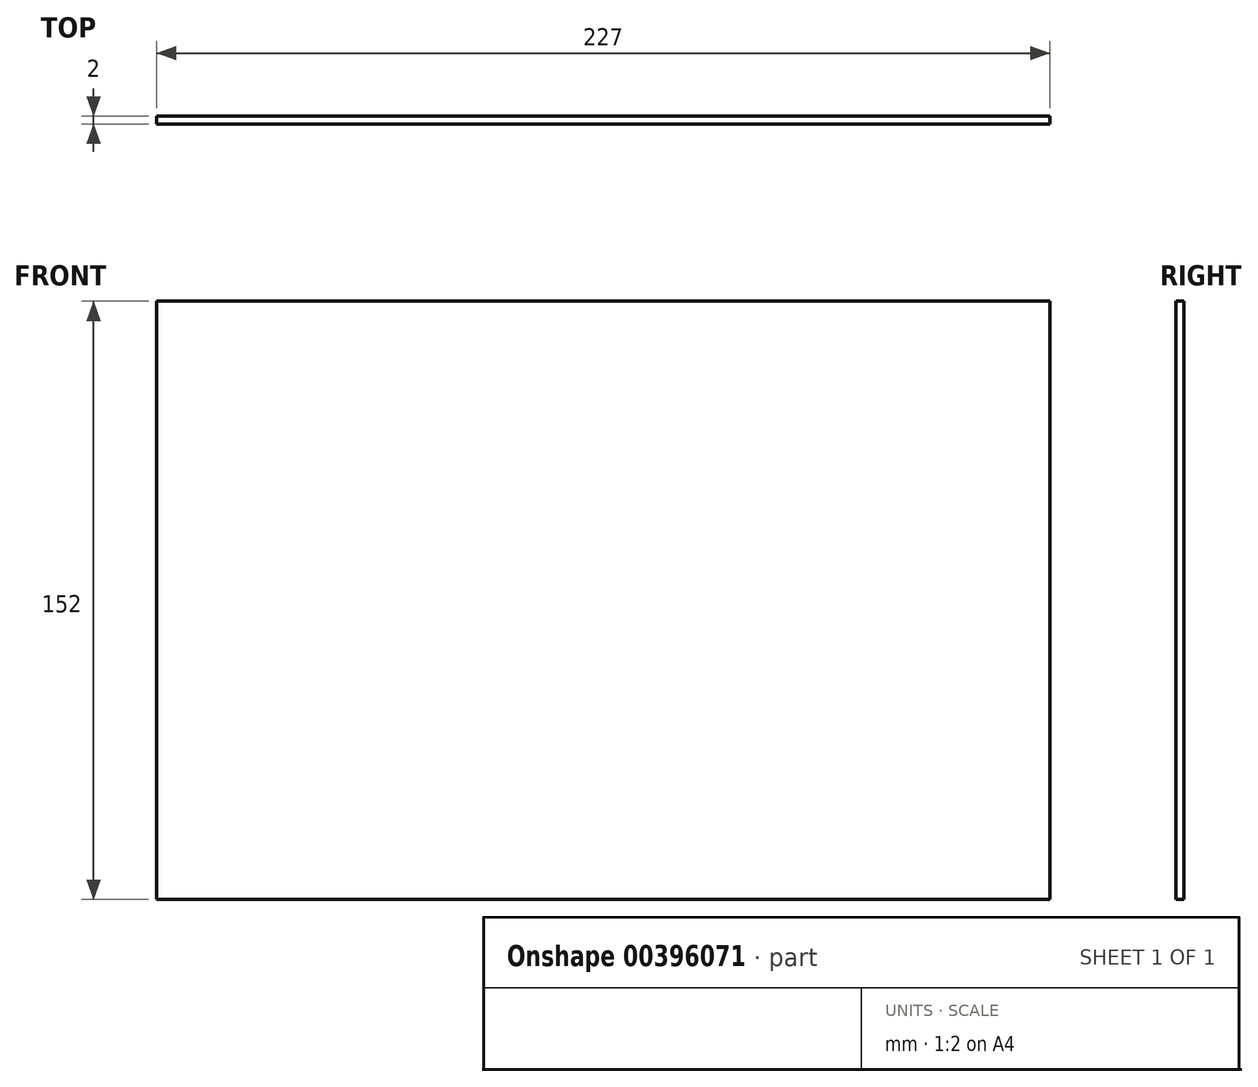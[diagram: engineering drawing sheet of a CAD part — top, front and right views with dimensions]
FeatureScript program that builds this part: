
annotation { "Feature Type Name" : "Feature", "Feature Type Description" : "" }
export const myFeature = defineFeature(function(context is Context, id is Id, definition is map)
    precondition{}
    {
        {
            var Q0;
            Q0=qCreatedBy(makeId("Front.planeOp"),FACE);
            var sketch = newSketch(context, id + "F0", { "sketchPlane" : qUnion([Q0])});
            skLineSegment(sketch, "E0.bottom", {"start": v(-113.5, 76) * mm, "end": v(113.5, 76) * mm});
            skLineSegment(sketch, "E0.top", {"start": v(-113.5, -76) * mm, "end": v(113.5, -76) * mm});
            skLineSegment(sketch, "E0.left", {"start": v(-113.5, 76) * mm, "end": v(-113.5, -76) * mm});
            skLineSegment(sketch, "E0.right", {"start": v(113.5, 76) * mm, "end": v(113.5, -76) * mm});
            skPoint(sketch, "E0.middle", {"position": v(0, 0) * mm});
            skSolve(sketch);
        }
        {
            var Q0;
            Q0 = qSketchRegion(id + "F0", true);
            extrude(context, id + "F1", {"entities" : qUnion([Q0]), "depth" : 2 * mm});
        }
    });
